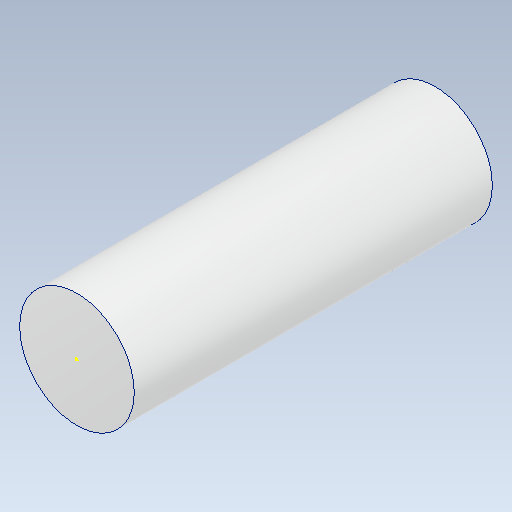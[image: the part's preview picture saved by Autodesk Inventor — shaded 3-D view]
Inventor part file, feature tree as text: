
AUTODESK INVENTOR PART (.ipt)
format: ipt  version: 2021 (Build 250183000, 183)  size: 104,448 bytes
history: native  units: mm
features: other x3, sketch x3
ambient origin geometry x8: Origin, YZ Plane, XZ Plane, XY Plane, X Axis, Y Axis, Z Axis, Center Point
bodies: Solid1 (feature_tree)
feature tree (6):
  other  "Rotatory Hinge 2.ipt"
  other  "Solid1::Rotatory Hinge 2.ipt"
  other  "TaggingFeature1"
  sketch  "Sketch1"  dims[d0=10.0mm]
  sketch  "Sketch2"
  sketch  "Sketch3"
